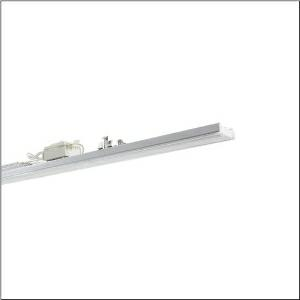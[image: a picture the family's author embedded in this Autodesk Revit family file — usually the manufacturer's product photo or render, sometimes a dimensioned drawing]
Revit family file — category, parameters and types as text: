
# Revit family: licross_r__21_recessed_mo_52tl18vn555g_0100
name_source: partatom
category: Lighting Fixtures
units: mm (PartAtom-declared; Revit-internal decimal feet)

## family parameters
Cut with Voids When Loaded = No
Host = Face
Light Source = No
Part Type = Normal
Room Calculation Point = No
Round Connector Dimension = Use Diameter
Shared = No

## types (1)
- --- (1 x LED, 5500 lm, 30.9 W, 5000K)
    Apparent Load = 31 VA
    CIE Flux Codes = 79 95 99 100 100
    Color Rendering = 80
    Color Temperature = 5000K
    Default Elevation = 1800 mm
    Description = Licross® 21 Recessed MO, luminaire insert, of sheet steel, galvanised, coil coated, white, length: 1.500mm, width: 66mm, height: 67mm, LED rated luminous flux: 5.500lm, light colour: 850, control gear: DALI 2, CLO, with plug, 5-pole, with phase selection, mains connection: 220..240V, AC, 50/60Hz, start of lifetime: 31W, end of service life: 37W, halogen-free wiring, primary optical cover: cover, of PMMA, light emission: direct distribution, primary light characteristic: symmetric, protection rating (complete): IP40, insulation class (complete): insulation class I (protective earthing), certification: CE, ENEC, VDE, UKCA, protection symbol: D if used in an environment without relevant dust loads with corresponding accessories, impact resistance: IK06, permissible ambient temperature for indoor applications: -25..+45°C, corresponds to IFS (International Featured Standards) requirements for safety and quality in the food industry, reducing of maximum allowable ambient temperature of 5°C with ceiling mounting, LABS conformity tested according to VDMA 24364:2018-05, packaging unit: 1 piece
    Height = 58 mm
    Lamp = 1 x LED
    Lamp Light Flux = 5500 lm
    Lamp Power = 30.9 W
    Lamp count = 1
    Length = 1500 mm
    Luminous efficacy = 178 lm/W
    Manufacturer = Siteco
    ModVariant = No
    Model = 52TL18VN555G
    Mounting Place = Ceiling
    Mounting Type = Pendant
    Number of Poles = 1
    OnlyDefault = Yes
    Power Factor = 1
    Product Name = Licross® 21 Recessed MO
    Product group = luminaire insert
    ProductGroupID = 901
    Protection Class = Protection class I
    Protection Degree = IP 40
    RLX_Detail_Level = 1
    RLX_Emergency_Light_Flux = 0 lm
    RLX_Emergency_Type = 0
    RLX_Emergency_Type_DB = No
    RlxData = <blob elided: 23961 chars, md5=2d6a1bcb>
    Socket = socket
    Standby Power = 0 W
    System Light Flux = 5500 lm
    System Power = 31 W
    Type Comments = factory setting: luminous flux: 100 % | dim-lin: 254 | 209 mA
    Type Image = l_1296930.jpg
    URL = http://relux.com
    VarID = @adj_079340
    Voltage = 0 V
    Weight = 0.00 kg
    Width = 66 mm

## geometry (parser evidence)
native form markers: Blend x4, Sweep x11
no freeform markers — native parametric forms only
